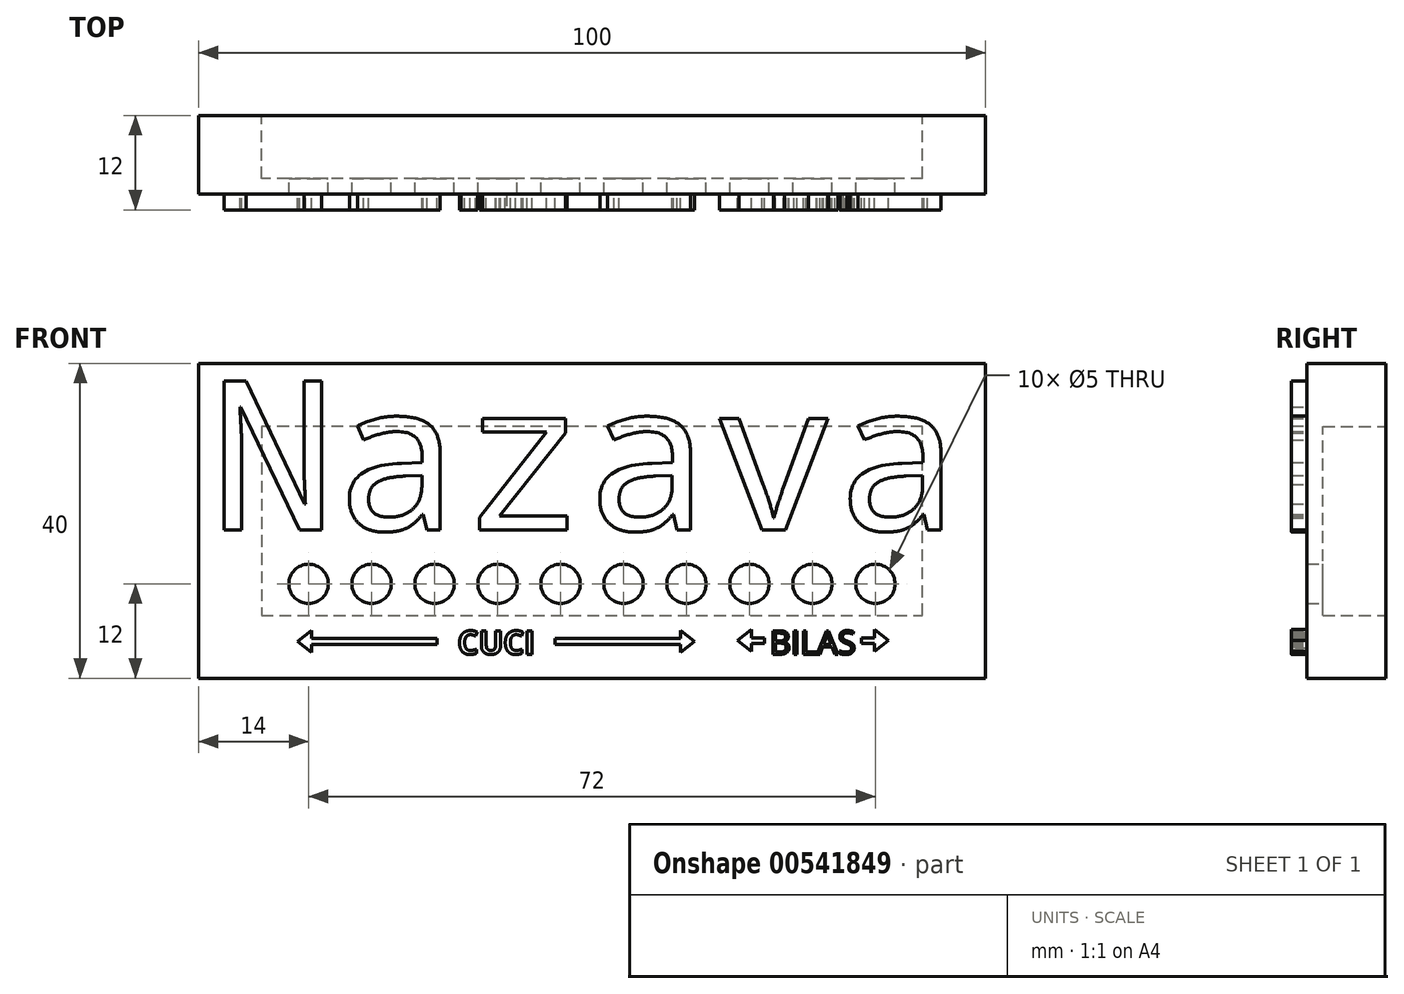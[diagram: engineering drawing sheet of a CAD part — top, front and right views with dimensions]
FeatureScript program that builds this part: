
annotation { "Feature Type Name" : "Feature", "Feature Type Description" : "" }
export const myFeature = defineFeature(function(context is Context, id is Id, definition is map)
    precondition{}
    {
        {
            var Q0;
            Q0=qCreatedBy(makeId("Front.planeOp"),FACE);
            var sketch = newSketch(context, id + "F0", { "sketchPlane" : qUnion([Q0])});
            skLineSegment(sketch, "E0.bottom", {"start": v(0, 0) * mm, "end": v(100, 0) * mm});
            skLineSegment(sketch, "E0.top", {"start": v(0, 40) * mm, "end": v(100, 40) * mm});
            skLineSegment(sketch, "E0.left", {"start": v(0, 0) * mm, "end": v(0, 40) * mm});
            skLineSegment(sketch, "E0.right", {"start": v(100, 0) * mm, "end": v(100, 40) * mm});
            skCircle(sketch, "E1", {"center": v(14, 12) * mm, "radius": 2.5 * mm});
            skCircle(sketch, "E2.1.0.0", {"center": v(22, 12) * mm, "radius": 2.5 * mm});
            skCircle(sketch, "E2.2.0.0", {"center": v(30, 12) * mm, "radius": 2.5 * mm});
            skCircle(sketch, "E2.3.0.0", {"center": v(38, 12) * mm, "radius": 2.5 * mm});
            skCircle(sketch, "E2.4.0.0", {"center": v(46, 12) * mm, "radius": 2.5 * mm});
            skCircle(sketch, "E2.5.0.0", {"center": v(54, 12) * mm, "radius": 2.5 * mm});
            skCircle(sketch, "E2.6.0.0", {"center": v(62, 12) * mm, "radius": 2.5 * mm});
            skCircle(sketch, "E2.7.0.0", {"center": v(70, 12) * mm, "radius": 2.5 * mm});
            skCircle(sketch, "E2.8.0.0", {"center": v(78, 12) * mm, "radius": 2.5 * mm});
            skCircle(sketch, "E2.9.0.0", {"center": v(86, 12) * mm, "radius": 2.5 * mm});
            skLineSegment(sketch, "E2.direction1", {"start": v(14, 12) * mm, "end": v(22, 12) * mm, "construction": true});
            skSolve(sketch);
        }
        {
            var Q0;
            Q0=makeQuery(id+"F0.imprint","IMPRINT",FACE,{"disambiguationData":[TD([[makeQuery(id+"F0.imprint","IMPRINT",EDGE,{"derivedFrom":sQuery(id+"F0.wireOp",EDGE,"E0.bottom")}),1.0]])]});
            extrude(context, id + "F1", {"entities" : qUnion([Q0]), "flatOperationType" : FlatOperationType.REMOVE, "depth" : 10 * mm, "offsetDistance" : 25 * mm, "domain" : OperationDomain.MODEL});
        }
        {
            var Q0;
            Q0=qCreatedBy(makeId("Front.planeOp"),FACE);
            var sketch = newSketch(context, id + "F2", { "sketchPlane" : qUnion([Q0])});
            skLineSegment(sketch, "E3.0", {"start": v(92, 32) * mm, "end": v(8, 32) * mm});
            skLineSegment(sketch, "E3.1", {"start": v(92, 8) * mm, "end": v(92, 32) * mm});
            skLineSegment(sketch, "E3.2", {"start": v(8, 8) * mm, "end": v(92, 8) * mm});
            skLineSegment(sketch, "E3.3", {"start": v(8, 32) * mm, "end": v(8, 8) * mm});
            skSolve(sketch);
        }
        {
            var Q0;
            Q0=makeQuery(id+"F2.imprint","IMPRINT",FACE,{"disambiguationData":[TD([[makeQuery(id+"F2.imprint","IMPRINT",EDGE,{"derivedFrom":sQuery(id+"F2.wireOp",EDGE,"E3.0")}),1.0]])]});
            extrude(context, id + "F3", {"entities" : qUnion([Q0]), "operationType" : NewBodyOperationType.REMOVE, "depth" : 8 * mm, "offsetDistance" : 25 * mm});
        }
        {
            var Q0;
            Q0=makeQuery(id+"F1.opExtrude","CAP_FACE",FACE,{"disambiguationData":[OSD([sQuery(id+"F0.wireOp",EDGE,"E0.bottom"),sQuery(id+"F0.wireOp",EDGE,"E0.top"),sQuery(id+"F0.wireOp",EDGE,"E0.left"),sQuery(id+"F0.wireOp",EDGE,"E0.right"),sQuery(id+"F0.wireOp",EDGE,"E1"),sQuery(id+"F0.wireOp",EDGE,"E2.1.0.0"),sQuery(id+"F0.wireOp",EDGE,"E2.2.0.0"),sQuery(id+"F0.wireOp",EDGE,"E2.3.0.0"),sQuery(id+"F0.wireOp",EDGE,"E2.4.0.0"),sQuery(id+"F0.wireOp",EDGE,"E2.5.0.0"),sQuery(id+"F0.wireOp",EDGE,"E2.6.0.0"),sQuery(id+"F0.wireOp",EDGE,"E2.7.0.0"),sQuery(id+"F0.wireOp",EDGE,"E2.8.0.0"),sQuery(id+"F0.wireOp",EDGE,"E2.9.0.0")])],"isStart":false});
            var sketch = newSketch(context, id + "F4", { "sketchPlane" : qUnion([Q0])});
            skText(sketch, "E4", { "text": "Nazava", "fontName": "DroidSansMono.ttf"});
            const initialGuessF4  = {"E4": [0.00153, 0.01883, 1, 0, 0.01908]};
            skSetInitialGuess(sketch, initialGuessF4);
            skSolve(sketch);
        }
        {
            var Q0;
            Q0 = qSketchRegion(id + "F4", true);
            extrude(context, id + "F5", {"entities" : qUnion([Q0]), "operationType" : NewBodyOperationType.ADD, "depth" : 2 * mm, "offsetDistance" : 25 * mm});
        }
        {
            var Q0;
            {var subQ0=sQuery(id+"F0.wireOp",EDGE,"E2.9.0.0");var subQ1=sQuery(id+"F0.wireOp",EDGE,"E2.8.0.0");var subQ2=sQuery(id+"F0.wireOp",EDGE,"E2.7.0.0");var subQ3=sQuery(id+"F0.wireOp",EDGE,"E2.6.0.0");var subQ4=sQuery(id+"F0.wireOp",EDGE,"E0.left");var subQ5=sQuery(id+"F0.wireOp",EDGE,"E0.top");var subQ6=sQuery(id+"F0.wireOp",EDGE,"E0.right");var subQ7=sQuery(id+"F0.wireOp",EDGE,"E0.bottom");var subQ8=sQuery(id+"F0.wireOp",EDGE,"E2.5.0.0");var subQ9=sQuery(id+"F0.wireOp",EDGE,"E1");var subQ10=sQuery(id+"F0.wireOp",EDGE,"E2.1.0.0");var subQ11=sQuery(id+"F0.wireOp",EDGE,"E2.2.0.0");var subQ12=sQuery(id+"F0.wireOp",EDGE,"E2.3.0.0");var subQ13=sQuery(id+"F0.wireOp",EDGE,"E2.4.0.0");Q0=makeQuery(id+"F5.boolean.opBoolean","SPLIT",FACE,{"disambiguationData":[TD([makeQuery(id+"F1.opExtrude","SWEPT_FACE",FACE,{"disambiguationData":[OSD([subQ7])]})])],"derivedFrom":makeQuery(id+"F1.opExtrude","CAP_FACE",FACE,{"disambiguationData":[OSD([subQ7,subQ5,subQ4,subQ6,subQ9,subQ10,subQ11,subQ12,subQ13,subQ8,subQ3,subQ2,subQ1,subQ0])],"isStart":false})});}
            var sketch = newSketch(context, id + "F6", { "sketchPlane" : qUnion([Q0])});
            skText(sketch, "E5", { "text": "CUCI", "fontName": "OpenSans-Bold.ttf"});
            skText(sketch, "E6", { "text": "BILAS", "fontName": "OpenSans-Regular.ttf"});
            skLineSegment(sketch, "E7.bottom", {"start": v(45.3, 5.04) * mm, "end": v(61.22, 5.04) * mm});
            skLineSegment(sketch, "E7.top", {"start": v(45.3, 4.33) * mm, "end": v(61.22, 4.33) * mm});
            skLineSegment(sketch, "E7.left", {"start": v(45.3, 5.04) * mm, "end": v(45.3, 4.33) * mm});
            skLineSegment(sketch, "E8", {"start": v(61.22, 5.04) * mm, "end": v(61.22, 6.09) * mm});
            skLineSegment(sketch, "E9", {"start": v(61.22, 6.09) * mm, "end": v(62.99, 4.68) * mm});
            skLineSegment(sketch, "E10", {"start": v(62.99, 4.68) * mm, "end": v(61.22, 3.31) * mm});
            skLineSegment(sketch, "E11", {"start": v(61.22, 3.31) * mm, "end": v(61.22, 4.33) * mm});
            skLineSegment(sketch, "E12.bottom", {"start": v(84.2, 5.16) * mm, "end": v(85.89, 5.16) * mm});
            skLineSegment(sketch, "E12.top", {"start": v(84.2, 4.45) * mm, "end": v(85.89, 4.45) * mm});
            skLineSegment(sketch, "E12.left", {"start": v(84.2, 5.16) * mm, "end": v(84.2, 4.45) * mm});
            skLineSegment(sketch, "E13", {"start": v(85.89, 5.16) * mm, "end": v(85.89, 6.21) * mm});
            skLineSegment(sketch, "E14", {"start": v(85.89, 6.21) * mm, "end": v(87.65, 4.8) * mm});
            skLineSegment(sketch, "E15", {"start": v(87.65, 4.8) * mm, "end": v(85.89, 3.44) * mm});
            skLineSegment(sketch, "E16", {"start": v(85.89, 3.44) * mm, "end": v(85.89, 4.45) * mm});
            skPoint(sketch, "E17", {"position": v(85.04, 4.45) * mm});
            skLineSegment(sketch, "E18.MirrorCS", {"start": v(71.93, 5.16) * mm, "end": v(71.93, 4.45) * mm});
            skLineSegment(sketch, "E19.MirrorCS", {"start": v(71.93, 4.45) * mm, "end": v(70.24, 4.45) * mm});
            skLineSegment(sketch, "E20.MirrorCS", {"start": v(71.93, 5.16) * mm, "end": v(70.24, 5.16) * mm});
            skPoint(sketch, "E21.MirrorP", {"position": v(71.09, 4.45) * mm});
            skLineSegment(sketch, "E22.MirrorCS", {"start": v(68.48, 4.8) * mm, "end": v(70.24, 3.44) * mm});
            skLineSegment(sketch, "E23.MirrorCS", {"start": v(70.24, 5.16) * mm, "end": v(70.24, 6.21) * mm});
            skLineSegment(sketch, "E24.MirrorCS", {"start": v(70.24, 6.21) * mm, "end": v(68.48, 4.8) * mm});
            skLineSegment(sketch, "E25.MirrorCS", {"start": v(70.24, 3.44) * mm, "end": v(70.24, 4.45) * mm});
            skLineSegment(sketch, "E26.MirrorCS", {"start": v(14.36, 3.31) * mm, "end": v(14.36, 4.33) * mm});
            skLineSegment(sketch, "E27.MirrorCS", {"start": v(30.3, 5.04) * mm, "end": v(30.3, 4.33) * mm});
            skLineSegment(sketch, "E28.MirrorCS", {"start": v(14.36, 5.04) * mm, "end": v(14.36, 6.09) * mm});
            skLineSegment(sketch, "E29.MirrorCS", {"start": v(30.3, 5.04) * mm, "end": v(14.36, 5.04) * mm});
            skLineSegment(sketch, "E30.MirrorCS", {"start": v(30.3, 4.33) * mm, "end": v(14.36, 4.33) * mm});
            skLineSegment(sketch, "E31.MirrorCS", {"start": v(12.6, 4.68) * mm, "end": v(14.36, 3.31) * mm});
            skLineSegment(sketch, "E32.MirrorCS", {"start": v(14.36, 6.09) * mm, "end": v(12.6, 4.68) * mm});
            const initialGuessF6  = {"E5": [0.03293, 0.00306, 1, 0, 0.003], "E6": [0.07256, 0.00306, 1, 0, 0.003]};
            skSetInitialGuess(sketch, initialGuessF6);
            skSolve(sketch);
        }
        {
            var Q0;
            Q0 = qSketchRegion(id + "F6", true);
            extrude(context, id + "F7", {"entities" : qUnion([Q0]), "operationType" : NewBodyOperationType.ADD, "depth" : 2 * mm, "offsetDistance" : 25 * mm});
        }
    });
